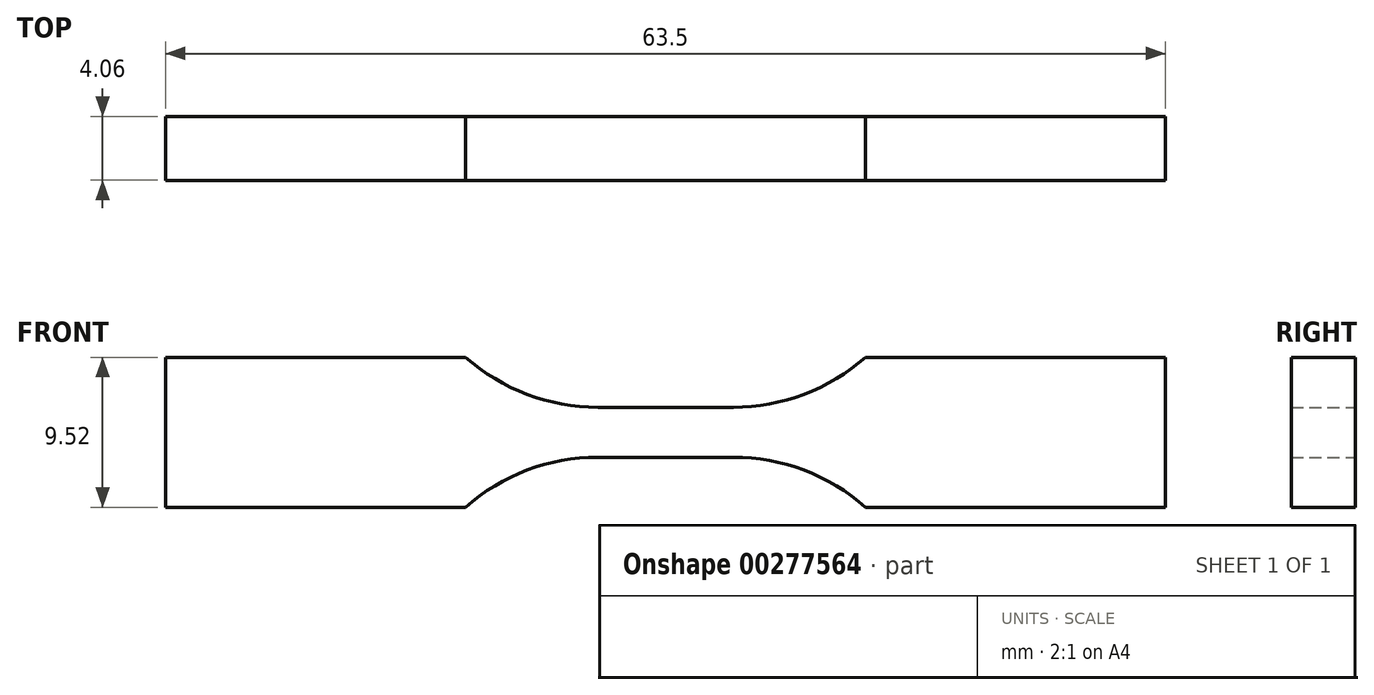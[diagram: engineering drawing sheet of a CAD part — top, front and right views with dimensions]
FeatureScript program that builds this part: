
annotation { "Feature Type Name" : "Feature", "Feature Type Description" : "" }
export const myFeature = defineFeature(function(context is Context, id is Id, definition is map)
    precondition{}
    {
        {
            var Q0;
            Q0=qCreatedBy(makeId("Front.planeOp"),FACE);
            var sketch = newSketch(context, id + "F0", { "sketchPlane" : qUnion([Q0])});
            skLineSegment(sketch, "E0", {"start": v(0, 1.59) * mm, "end": v(4.3, 1.59) * mm});
            skArc(sketch, "E1", {"start": v(4.3, 1.59) * mm, "mid": v(8.79, 2.4) * mm, "end": v(12.7, 4.76) * mm});
            skLineSegment(sketch, "E2", {"start": v(12.7, 4.76) * mm, "end": v(31.75, 4.76) * mm});
            skLineSegment(sketch, "E3", {"start": v(31.75, 4.76) * mm, "end": v(31.75, 0) * mm});
            skLineSegment(sketch, "E4.MirrorCS", {"start": v(0, -1.59) * mm, "end": v(4.3, -1.59) * mm});
            skLineSegment(sketch, "E5.MirrorCS", {"start": v(31.75, -4.76) * mm, "end": v(31.75, 0) * mm});
            skLineSegment(sketch, "E6.MirrorCS", {"start": v(12.7, -4.76) * mm, "end": v(31.75, -4.76) * mm});
            skArc(sketch, "E7.MirrorCS", {"start": v(4.3, -1.59) * mm, "mid": v(8.79, -2.4) * mm, "end": v(12.7, -4.76) * mm});
            skArc(sketch, "E8.MirrorCS", {"start": v(-4.3, -1.59) * mm, "mid": v(-8.79, -2.4) * mm, "end": v(-12.7, -4.76) * mm});
            skLineSegment(sketch, "E9.MirrorCS", {"start": v(-12.7, -4.76) * mm, "end": v(-31.75, -4.76) * mm});
            skArc(sketch, "E10.MirrorCS", {"start": v(-4.3, 1.59) * mm, "mid": v(-8.79, 2.4) * mm, "end": v(-12.7, 4.76) * mm});
            skLineSegment(sketch, "E11.MirrorCS", {"start": v(-12.7, 4.76) * mm, "end": v(-31.75, 4.76) * mm});
            skLineSegment(sketch, "E12.MirrorCS", {"start": v(-31.75, -4.76) * mm, "end": v(-31.75, 0) * mm});
            skLineSegment(sketch, "E13.MirrorCS", {"start": v(0, -1.59) * mm, "end": v(-4.3, -1.59) * mm});
            skLineSegment(sketch, "E14.MirrorCS", {"start": v(-31.75, 4.76) * mm, "end": v(-31.75, 0) * mm});
            skLineSegment(sketch, "E15.MirrorCS", {"start": v(0, 1.59) * mm, "end": v(-4.3, 1.59) * mm});
            skSolve(sketch);
        }
        {
            var Q0;
            Q0=makeQuery(id+"F0.imprint","IMPRINT",FACE,{"disambiguationData":[TD([[makeQuery(id+"F0.imprint","IMPRINT",EDGE,{"derivedFrom":sQuery(id+"F0.wireOp",EDGE,"E0")}),-1.0]])]});
            extrude(context, id + "F1", {"entities" : qUnion([Q0]), "depth" : 4.06 * mm});
        }
    });
